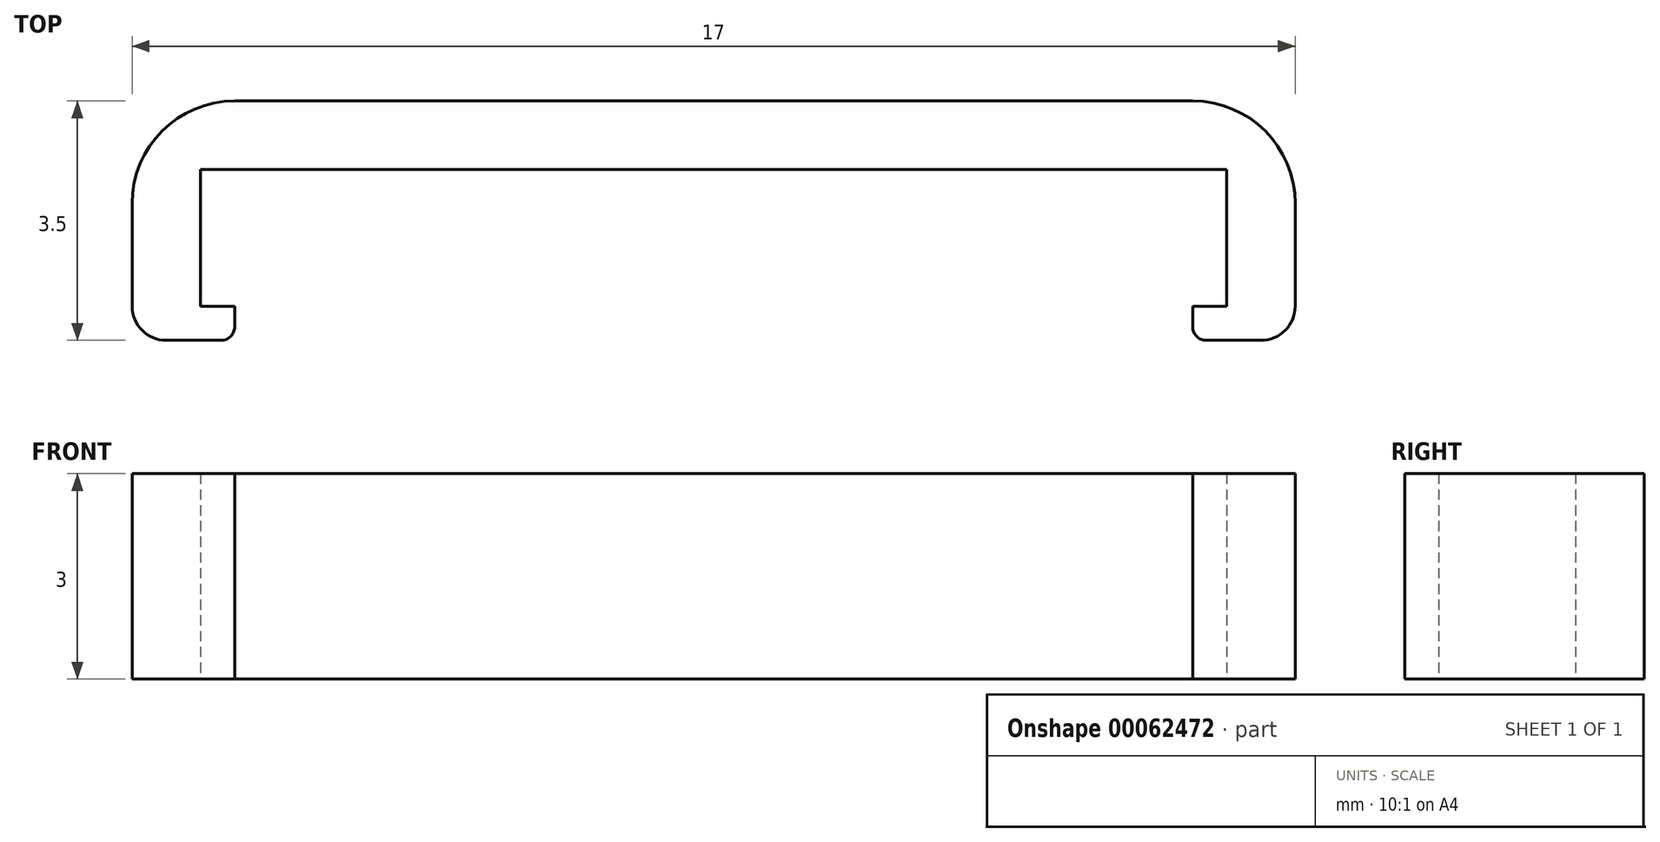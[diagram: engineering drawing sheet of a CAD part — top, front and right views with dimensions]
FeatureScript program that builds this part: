
annotation { "Feature Type Name" : "Feature", "Feature Type Description" : "" }
export const myFeature = defineFeature(function(context is Context, id is Id, definition is map)
    precondition{}
    {
        {
            var Q0;
            Q0=qCreatedBy(makeId("Top.planeOp"),FACE);
            var sketch = newSketch(context, id + "F0", { "sketchPlane" : qUnion([Q0])});
            skLineSegment(sketch, "E0", {"start": v(0, 0) * mm, "end": v(7.5, 0) * mm});
            skLineSegment(sketch, "E1", {"start": v(7.5, 0) * mm, "end": v(7.5, -2) * mm});
            skLineSegment(sketch, "E2", {"start": v(7.5, -2) * mm, "end": v(7, -2) * mm});
            skLineSegment(sketch, "E3", {"start": v(7, -2) * mm, "end": v(7, -2.3) * mm});
            skLineSegment(sketch, "E4", {"start": v(7.2, -2.5) * mm, "end": v(7.5, -2.5) * mm});
            skLineSegment(sketch, "E5", {"start": v(7.5, -2.5) * mm, "end": v(8, -2.5) * mm});
            skLineSegment(sketch, "E6", {"start": v(8.5, -2) * mm, "end": v(8.5, -0.5) * mm});
            skLineSegment(sketch, "E7", {"start": v(7, 1) * mm, "end": v(0, 1) * mm});
            skPoint(sketch, "E8.orphan", {"position": v(8.5, 0) * mm});
            skPoint(sketch, "E9.visualSharp", {"position": v(8.5, 1) * mm});
            skArc(sketch, "E9.filletArc", {"start": v(8.5, -0.5) * mm, "mid": v(8.06, 0.56) * mm, "end": v(7, 1) * mm});
            skPoint(sketch, "E10.visualSharp", {"position": v(7, -2.5) * mm});
            skArc(sketch, "E10.filletArc", {"start": v(7, -2.3) * mm, "mid": v(7.06, -2.44) * mm, "end": v(7.2, -2.5) * mm});
            skPoint(sketch, "E11.visualSharp", {"position": v(8.5, -2.5) * mm});
            skArc(sketch, "E11.filletArc", {"start": v(8, -2.5) * mm, "mid": v(8.35, -2.35) * mm, "end": v(8.5, -2) * mm});
            skArc(sketch, "E12.MirrorCS", {"start": v(-7, -2.3) * mm, "mid": v(-7.06, -2.44) * mm, "end": v(-7.2, -2.5) * mm});
            skLineSegment(sketch, "E13.MirrorCS", {"start": v(-7.2, -2.5) * mm, "end": v(-7.5, -2.5) * mm});
            skLineSegment(sketch, "E14.MirrorCS", {"start": v(-7.5, -2.5) * mm, "end": v(-8, -2.5) * mm});
            skLineSegment(sketch, "E15.MirrorCS", {"start": v(-7, -2) * mm, "end": v(-7, -2.3) * mm});
            skLineSegment(sketch, "E16.MirrorCS", {"start": v(-7.5, -2) * mm, "end": v(-7, -2) * mm});
            skArc(sketch, "E17.MirrorCS", {"start": v(-8, -2.5) * mm, "mid": v(-8.35, -2.35) * mm, "end": v(-8.5, -2) * mm});
            skArc(sketch, "E18.MirrorCS", {"start": v(-8.5, -0.5) * mm, "mid": v(-8.06, 0.56) * mm, "end": v(-7, 1) * mm});
            skLineSegment(sketch, "E19.MirrorCS", {"start": v(-7, 1) * mm, "end": v(0, 1) * mm});
            skPoint(sketch, "E20.MirrorP", {"position": v(-8.5, 0) * mm});
            skPoint(sketch, "E21.MirrorP", {"position": v(-8.5, 1) * mm});
            skPoint(sketch, "E22.MirrorP", {"position": v(-7, -2.5) * mm});
            skLineSegment(sketch, "E23.MirrorCS", {"start": v(0, 0) * mm, "end": v(-7.5, 0) * mm});
            skLineSegment(sketch, "E24.MirrorCS", {"start": v(-8.5, -2) * mm, "end": v(-8.5, -0.5) * mm});
            skLineSegment(sketch, "E25.MirrorCS", {"start": v(-7.5, 0) * mm, "end": v(-7.5, -2) * mm});
            skPoint(sketch, "E26.MirrorP", {"position": v(-8.5, -2.5) * mm});
            skSolve(sketch);
        }
        {
            var Q0;
            Q0=makeQuery(id+"F0.imprint","IMPRINT",FACE,{"disambiguationData":[TD([[makeQuery(id+"F0.imprint","IMPRINT",EDGE,{"derivedFrom":sQuery(id+"F0.wireOp",EDGE,"E0")}),1.0]])]});
            extrude(context, id + "F1", {"entities" : qUnion([Q0]), "depth" : 3 * mm});
        }
    });
